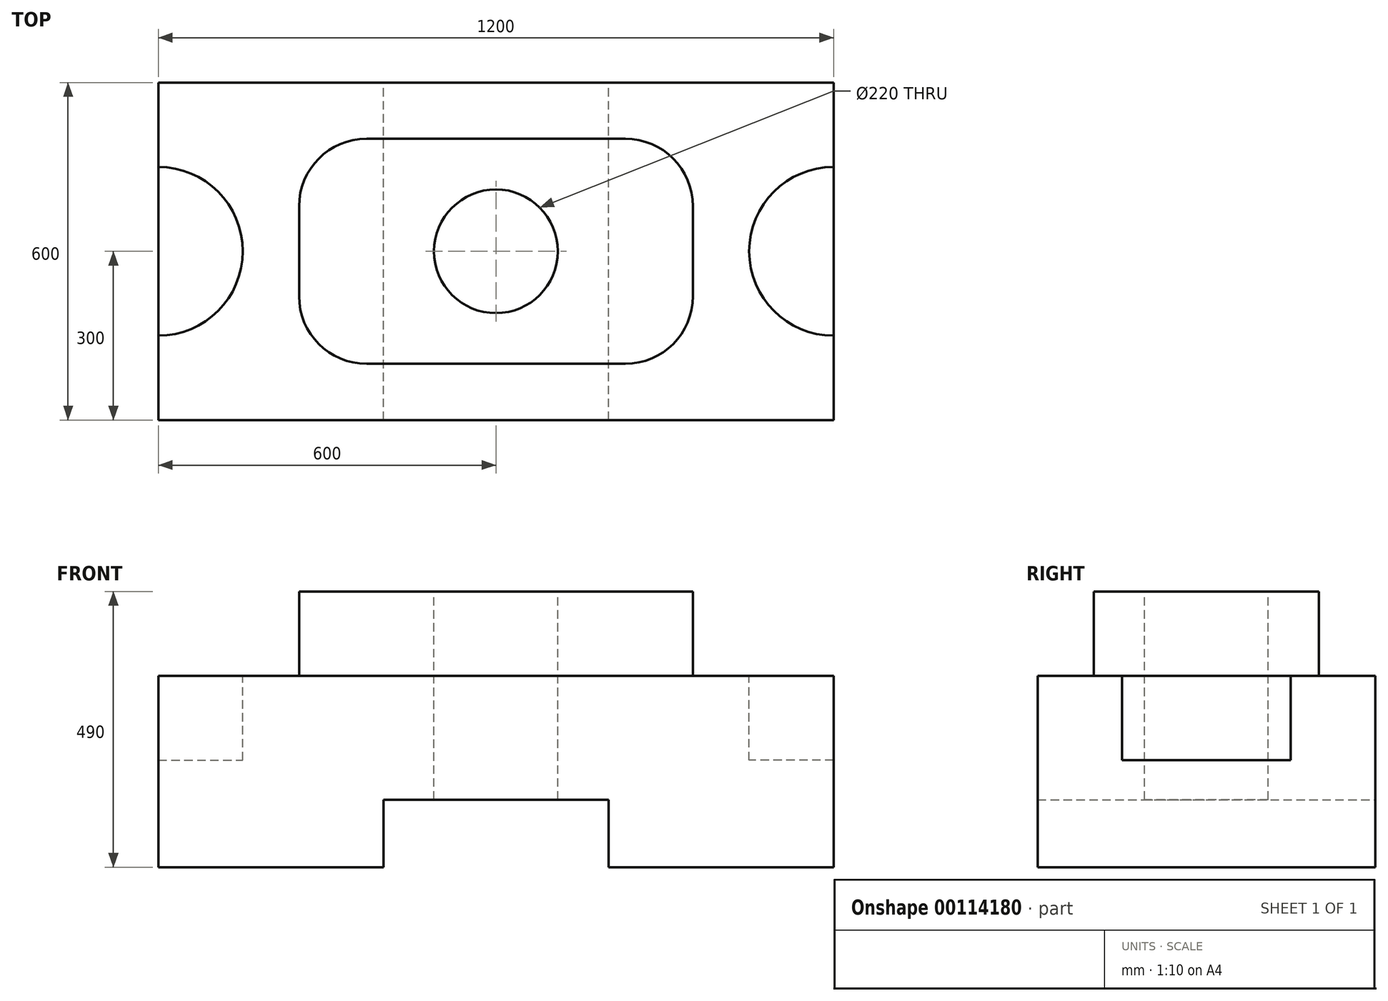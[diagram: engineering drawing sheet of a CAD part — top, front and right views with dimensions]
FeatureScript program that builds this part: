
annotation { "Feature Type Name" : "Feature", "Feature Type Description" : "" }
export const myFeature = defineFeature(function(context is Context, id is Id, definition is map)
    precondition{}
    {
        {
            var Q0;
            Q0=qCreatedBy(makeId("Front.planeOp"),FACE);
            var sketch = newSketch(context, id + "F0", { "sketchPlane" : qUnion([Q0])});
            skLineSegment(sketch, "E0.bottom", {"start": v(600, 170) * mm, "end": v(-600, 170) * mm});
            skLineSegment(sketch, "E0.top", {"start": v(600, -170) * mm, "end": v(-600, -170) * mm});
            skLineSegment(sketch, "E0.left", {"start": v(600, 170) * mm, "end": v(600, -170) * mm});
            skLineSegment(sketch, "E0.right", {"start": v(-600, 170) * mm, "end": v(-600, -170) * mm});
            skPoint(sketch, "E0.middle", {"position": v(0, 0) * mm});
            skPoint(sketch, "E1.center.orphan", {"position": v(-600, 0) * mm});
            skPoint(sketch, "E2.center.orphan", {"position": v(600, 0) * mm});
            skSolve(sketch);
        }
        {
            var Q0;
            Q0=makeQuery(id+"F0.imprint","IMPRINT",FACE,{"disambiguationData":[TD([[makeQuery(id+"F0.imprint","IMPRINT",EDGE,{"derivedFrom":sQuery(id+"F0.wireOp",EDGE,"E0.bottom")}),1.0]])]});
            extrude(context, id + "F1", {"entities" : qUnion([Q0]), "depth" : 600 * mm});
        }
        {
            var Q0;
            Q0=makeQuery(id+"F1.opExtrude","SWEPT_FACE",FACE,{"disambiguationData":[OSD([sQuery(id+"F0.wireOp",EDGE,"E0.bottom")])]});
            var sketch = newSketch(context, id + "F2", { "sketchPlane" : qUnion([Q0])});
            skArc(sketch, "E3", {"start": v(-600, -450) * mm, "mid": v(-450, -300) * mm, "end": v(-600, -150) * mm});
            skArc(sketch, "E4", {"start": v(600, -150) * mm, "mid": v(450, -300) * mm, "end": v(600, -450) * mm});
            skSolve(sketch);
        }
        {
            var Q0;
            {var subQ0=sQuery(id+"F2.wireOp",EDGE,"E3");Q0=makeQuery(id+"F2.imprint","IMPRINT",FACE,{"disambiguationData":[TD([[makeQuery(id+"F2.imprint","IMPRINT",EDGE,{"derivedFrom":subQ0}),1.0]])]});}
            var Q1;
            {var subQ0=sQuery(id+"F2.wireOp",EDGE,"E4");Q1=makeQuery(id+"F2.imprint","IMPRINT",FACE,{"disambiguationData":[TD([[makeQuery(id+"F2.imprint","IMPRINT",EDGE,{"derivedFrom":subQ0}),1.0]])]});}
            extrude(context, id + "F3", {"entities" : qUnion([Q0, Q1]), "operationType" : NewBodyOperationType.REMOVE, "oppositeDirection" : true, "depth" : 150 * mm});
        }
        {
            var Q0;
            Q0=makeQuery(id+"F1.opExtrude","CAP_FACE",FACE,{"disambiguationData":[OSD([sQuery(id+"F0.wireOp",EDGE,"E0.bottom"),sQuery(id+"F0.wireOp",EDGE,"E0.top"),sQuery(id+"F0.wireOp",EDGE,"E0.left"),sQuery(id+"F0.wireOp",EDGE,"E0.right")])],"isStart":true});
            var sketch = newSketch(context, id + "F4", { "sketchPlane" : qUnion([Q0])});
            skLineSegment(sketch, "E5.bottom", {"start": v(200, -50) * mm, "end": v(-200, -50) * mm});
            skLineSegment(sketch, "E5.left", {"start": v(200, -50) * mm, "end": v(200, -170) * mm});
            skLineSegment(sketch, "E5.right", {"start": v(-200, -50) * mm, "end": v(-200, -170) * mm});
            skPoint(sketch, "E5.middle", {"position": v(0, -170) * mm});
            skPoint(sketch, "E6.orphan", {"position": v(-200, -290) * mm});
            skPoint(sketch, "E7.orphan", {"position": v(200, -290) * mm});
            skSolve(sketch);
        }
        {
            var Q0;
            Q0=makeQuery(id+"F4.imprint","IMPRINT",FACE,{"disambiguationData":[TD([[makeQuery(id+"F4.imprint","IMPRINT",EDGE,{"derivedFrom":sQuery(id+"F4.wireOp",EDGE,"E5.bottom")}),1.0]])]});
            var Q1;
            Q1 = qSketchRegion(id + "F6", true);
            extrude(context, id + "F5", {"entities" : qUnion([Q0, Q1]), "operationType" : NewBodyOperationType.REMOVE, "endBound" : BoundingType.THROUGH_ALL, "oppositeDirection" : true, "depth" : 25 * mm});
        }
        {
            var Q0;
            Q0=makeQuery(id+"F1.opExtrude","SWEPT_FACE",FACE,{"disambiguationData":[OSD([sQuery(id+"F0.wireOp",EDGE,"E0.bottom")])]});
            var sketch = newSketch(context, id + "F6", { "sketchPlane" : qUnion([Q0])});
            skLineSegment(sketch, "E8.bottom", {"start": v(-230, -100) * mm, "end": v(230, -100) * mm});
            skLineSegment(sketch, "E8.top", {"start": v(-230, -500) * mm, "end": v(230, -500) * mm});
            skLineSegment(sketch, "E8.left", {"start": v(-350, -220) * mm, "end": v(-350, -380) * mm});
            skLineSegment(sketch, "E8.right", {"start": v(350, -220) * mm, "end": v(350, -380) * mm});
            skPoint(sketch, "E8.middle", {"position": v(0, -300) * mm});
            skPoint(sketch, "E8.middle.positionSnap0", {"position": v(-600, -300) * mm});
            skPoint(sketch, "E8.middle.positionSnap1", {"position": v(0, 0) * mm});
            skPoint(sketch, "E8.centerSnap0", {"position": v(-600, -300) * mm});
            skPoint(sketch, "E8.centerSnap1", {"position": v(0, 0) * mm});
            skPoint(sketch, "E9.visualSharp", {"position": v(350, -500) * mm});
            skArc(sketch, "E9.filletArc", {"start": v(230, -500) * mm, "mid": v(314.85, -464.85) * mm, "end": v(350, -380) * mm});
            skPoint(sketch, "E10.orphan", {"position": v(-600, 0) * mm});
            skPoint(sketch, "E11.left.start.orphan", {"position": v(-600, -600) * mm});
            skPoint(sketch, "E12.visualSharp", {"position": v(350, -100) * mm});
            skArc(sketch, "E12.filletArc", {"start": v(350, -220) * mm, "mid": v(314.85, -135.15) * mm, "end": v(230, -100) * mm});
            skPoint(sketch, "E13.visualSharp", {"position": v(-350, -100) * mm});
            skArc(sketch, "E13.filletArc", {"start": v(-230, -100) * mm, "mid": v(-314.85, -135.15) * mm, "end": v(-350, -220) * mm});
            skPoint(sketch, "E14.visualSharp", {"position": v(-350, -500) * mm});
            skArc(sketch, "E14.filletArc", {"start": v(-350, -380) * mm, "mid": v(-314.85, -464.85) * mm, "end": v(-230, -500) * mm});
            skSolve(sketch);
        }
        {
            var Q0;
            Q0=makeQuery(id+"F6.imprint","IMPRINT",FACE,{"disambiguationData":[TD([[makeQuery(id+"F6.imprint","IMPRINT",EDGE,{"derivedFrom":sQuery(id+"F6.wireOp",EDGE,"E8.bottom")}),-1.0]])]});
            extrude(context, id + "F7", {"entities" : qUnion([Q0]), "operationType" : NewBodyOperationType.ADD, "depth" : 150 * mm});
        }
        {
            var Q0;
            Q0=makeQuery(id+"F7.opExtrude","CAP_FACE",FACE,{"disambiguationData":[OSD([sQuery(id+"F6.wireOp",EDGE,"E8.bottom"),sQuery(id+"F6.wireOp",EDGE,"E8.top"),sQuery(id+"F6.wireOp",EDGE,"E8.left"),sQuery(id+"F6.wireOp",EDGE,"E8.right"),sQuery(id+"F6.wireOp",EDGE,"E9.filletArc"),sQuery(id+"F6.wireOp",EDGE,"E12.filletArc"),sQuery(id+"F6.wireOp",EDGE,"E13.filletArc"),sQuery(id+"F6.wireOp",EDGE,"E14.filletArc")])],"isStart":false});
            var sketch = newSketch(context, id + "F8", { "sketchPlane" : qUnion([Q0])});
            skCircle(sketch, "E15", {"center": v(0, -300) * mm, "radius": 110 * mm});
            skPoint(sketch, "E15.centerSnap0", {"position": v(0, -500) * mm});
            skPoint(sketch, "E15.centerSnap1", {"position": v(350, -300) * mm});
            skSolve(sketch);
        }
        {
            var Q0;
            Q0 = qSketchRegion(id + "F8", true);
            extrude(context, id + "F9", {"entities" : qUnion([Q0]), "operationType" : NewBodyOperationType.REMOVE, "endBound" : BoundingType.THROUGH_ALL, "oppositeDirection" : true, "depth" : 25 * mm});
        }
    });
